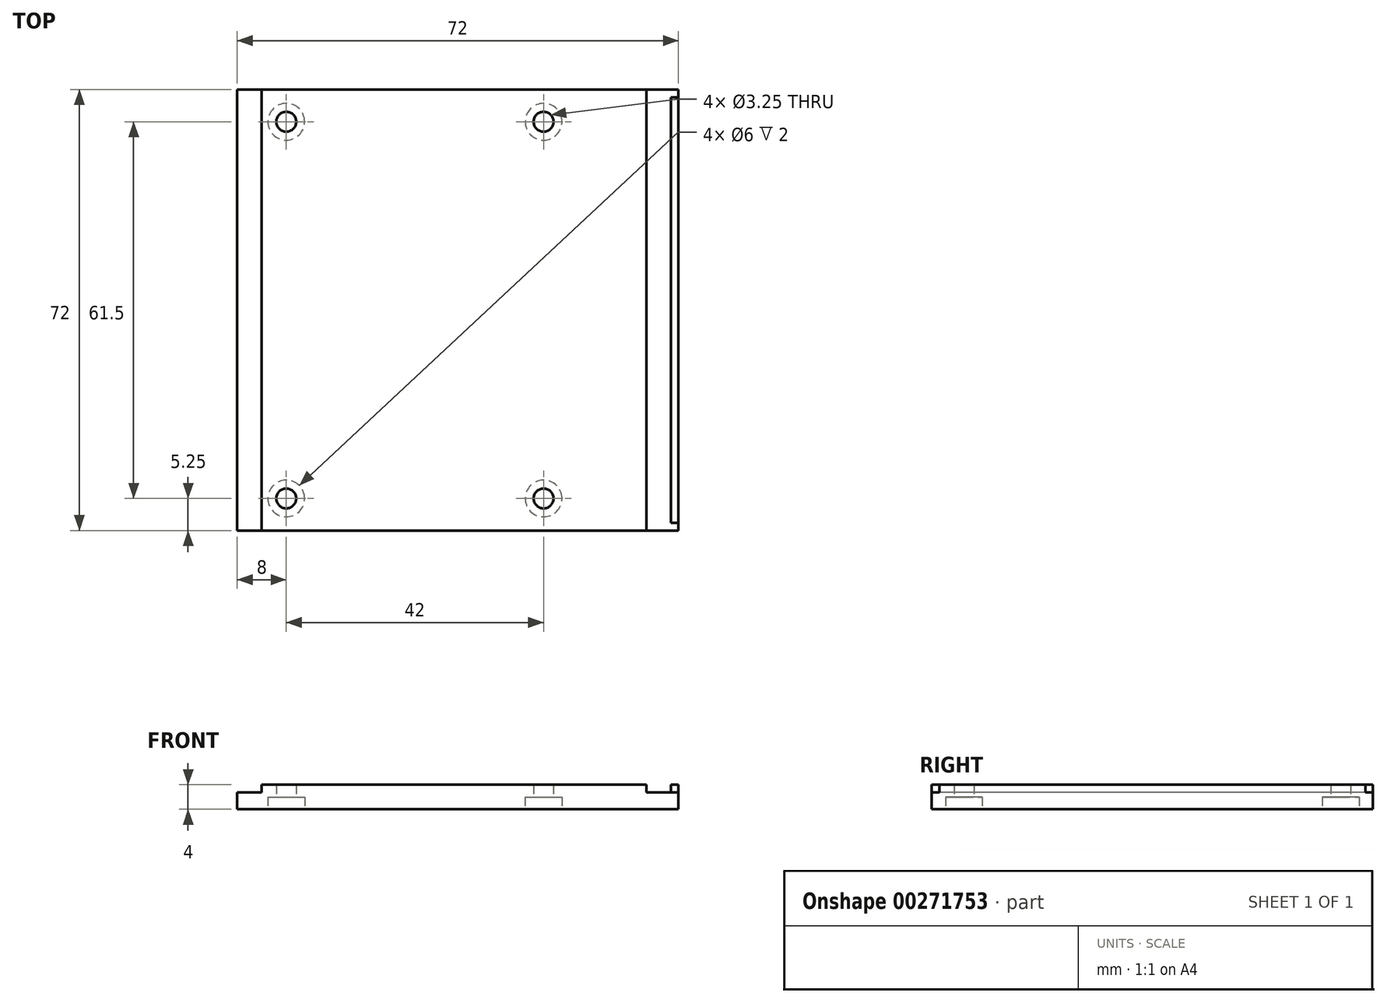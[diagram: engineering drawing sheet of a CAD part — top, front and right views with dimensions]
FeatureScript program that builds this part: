
annotation { "Feature Type Name" : "Feature", "Feature Type Description" : "" }
export const myFeature = defineFeature(function(context is Context, id is Id, definition is map)
    precondition{}
    {
        {
            var Q0;
            Q0=qCreatedBy(makeId("Top.planeOp"),FACE);
            var sketch = newSketch(context, id + "F0", { "sketchPlane" : qUnion([Q0])});
            skLineSegment(sketch, "E0.bottom", {"start": v(-36, 36) * mm, "end": v(36, 36) * mm});
            skLineSegment(sketch, "E0.top", {"start": v(-36, -36) * mm, "end": v(36, -36) * mm});
            skLineSegment(sketch, "E0.left", {"start": v(-36, 36) * mm, "end": v(-36, -36) * mm});
            skLineSegment(sketch, "E0.right", {"start": v(36, 36) * mm, "end": v(36, -36) * mm});
            skSolve(sketch);
        }
        {
            var Q0;
            Q0 = qSketchRegion(id + "F0", true);
            extrude(context, id + "F1", {"entities" : qUnion([Q0]), "depth" : 2.75 * mm});
        }
        {
            var Q0;
            Q0=makeQuery(id+"F1.opExtrude","CAP_FACE",FACE,{"disambiguationData":[OSD([sQuery(id+"F0.wireOp",EDGE,"E0.bottom"),sQuery(id+"F0.wireOp",EDGE,"E0.top"),sQuery(id+"F0.wireOp",EDGE,"E0.left"),sQuery(id+"F0.wireOp",EDGE,"E0.right")])],"isStart":false});
            var sketch = newSketch(context, id + "F2", { "sketchPlane" : qUnion([Q0])});
            skLineSegment(sketch, "E1.bottom", {"start": v(-32, 36) * mm, "end": v(30.75, 36) * mm});
            skLineSegment(sketch, "E1.top", {"start": v(-32, -36) * mm, "end": v(30.75, -36) * mm});
            skLineSegment(sketch, "E1.left", {"start": v(-32, 36) * mm, "end": v(-32, -36) * mm});
            skLineSegment(sketch, "E1.right", {"start": v(30.75, 36) * mm, "end": v(30.75, -36) * mm});
            skLineSegment(sketch, "E2.bottom", {"start": v(36, 36) * mm, "end": v(34.75, 36) * mm});
            skLineSegment(sketch, "E2.top", {"start": v(36, -36) * mm, "end": v(34.75, -36) * mm});
            skLineSegment(sketch, "E2.left", {"start": v(36, 36) * mm, "end": v(36, -36) * mm});
            skLineSegment(sketch, "E2.right", {"start": v(34.75, 36) * mm, "end": v(34.75, -36) * mm});
            skSolve(sketch);
        }
        {
            var Q0;
            Q0 = qSketchRegion(id + "F2", true);
            extrude(context, id + "F3", {"entities" : qUnion([Q0]), "operationType" : NewBodyOperationType.ADD, "depth" : 1.25 * mm});
        }
        {
            var Q0;
            Q0=makeQuery(id+"F1.opExtrude","CAP_FACE",FACE,{"disambiguationData":[OSD([sQuery(id+"F0.wireOp",EDGE,"E0.bottom"),sQuery(id+"F0.wireOp",EDGE,"E0.top"),sQuery(id+"F0.wireOp",EDGE,"E0.left"),sQuery(id+"F0.wireOp",EDGE,"E0.right")])],"isStart":true});
            var sketch = newSketch(context, id + "F4", { "sketchPlane" : qUnion([Q0])});
            skPoint(sketch, "E3", {"position": v(14, -30.75) * mm});
            skPoint(sketch, "E4", {"position": v(-28, -30.75) * mm});
            skPoint(sketch, "E5", {"position": v(14, 30.75) * mm});
            skPoint(sketch, "E6", {"position": v(-28, 30.75) * mm});
            skSolve(sketch);
        }
        {
            var Q0;
            Q0=sQuery(id+"F4.wireOp",VERTEX,"E4");
            var Q1;
            Q1=sQuery(id+"F4.wireOp",VERTEX,"E3");
            var Q2;
            Q2=sQuery(id+"F4.wireOp",VERTEX,"E6");
            var Q3;
            Q3=sQuery(id+"F4.wireOp",VERTEX,"E5");
            var Q4;
            Q4=makeQuery(id+"F1.opExtrude","SWEPT_BODY",BODY,{"disambiguationData":[OSD([sQuery(id+"F0.wireOp",EDGE,"E0.bottom"),sQuery(id+"F0.wireOp",EDGE,"E0.top"),sQuery(id+"F0.wireOp",EDGE,"E0.left"),sQuery(id+"F0.wireOp",EDGE,"E0.right")])]});
            hole(context, id + "F5", {"style" : HoleStyle.C_BORE, "endStyle" : HoleEndStyle.BLIND, "holeDiameter" : 3.25 * mm, "cBoreDiameter" : 6 * mm, "cBoreDepth" : 2 * mm, "holeDepth" : 8 * mm, "tappedDepth" : 12 * mm, "tapClearance" : 3, "startFromSketch" : true, "locations" : qUnion([Q0, Q1, Q2, Q3]), "scope" : qUnion([Q4])});
        }
        {
            var Q0;
            Q0=makeQuery(id+"F3.opExtrude","CAP_FACE",FACE,{"disambiguationData":[OSD([sQuery(id+"F2.wireOp",EDGE,"E2.bottom"),sQuery(id+"F2.wireOp",EDGE,"E2.top"),sQuery(id+"F2.wireOp",EDGE,"E2.left"),sQuery(id+"F2.wireOp",EDGE,"E2.right")])],"isStart":false});
            var sketch = newSketch(context, id + "F6", { "sketchPlane" : qUnion([Q0])});
            skLineSegment(sketch, "E7.bottom", {"start": v(34.75, 36) * mm, "end": v(36, 36) * mm});
            skLineSegment(sketch, "E7.top", {"start": v(34.75, 34.75) * mm, "end": v(36, 34.75) * mm});
            skLineSegment(sketch, "E7.left", {"start": v(34.75, 36) * mm, "end": v(34.75, 34.75) * mm});
            skLineSegment(sketch, "E7.right", {"start": v(36, 36) * mm, "end": v(36, 34.75) * mm});
            skLineSegment(sketch, "E8.bottom", {"start": v(36, -36) * mm, "end": v(34.75, -36) * mm});
            skLineSegment(sketch, "E8.top", {"start": v(36, -34.75) * mm, "end": v(34.75, -34.75) * mm});
            skLineSegment(sketch, "E8.left", {"start": v(36, -36) * mm, "end": v(36, -34.75) * mm});
            skLineSegment(sketch, "E8.right", {"start": v(34.75, -36) * mm, "end": v(34.75, -34.75) * mm});
            skSolve(sketch);
        }
        {
            var Q0;
            Q0 = qSketchRegion(id + "F6", true);
            extrude(context, id + "F7", {"entities" : qUnion([Q0]), "operationType" : NewBodyOperationType.REMOVE, "oppositeDirection" : true, "depth" : 1.25 * mm});
        }
    });
